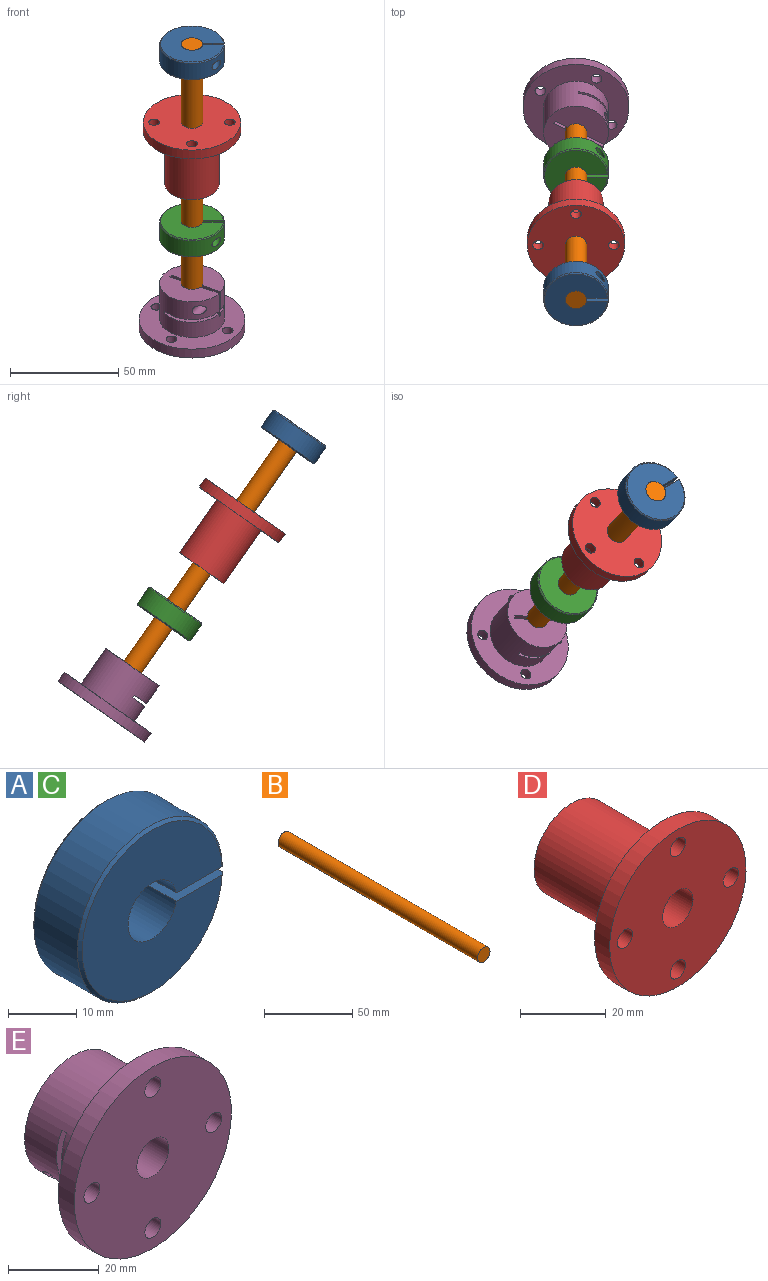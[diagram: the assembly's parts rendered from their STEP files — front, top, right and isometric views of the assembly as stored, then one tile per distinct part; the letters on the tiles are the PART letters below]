
ASSEMBLY  parts=5 mates=4
PART A: 10 faces, bbox 30x10x30 mm
  f0: cylinder r=5mm len=10mm, axis (0,-1,0), area 299.1mm2, adj f1,f3,f4,f5
  f1: plane 10.04x10mm, normal (0,0,1), area 87.6mm2, adj f0,f2,f4,f5,f7,f8,f9
  f2: cylinder r=15mm len=30mm, axis (0,-1,0), area 795.6mm2, adj f1,f3,f6,f7,f8,f9
  f3: plane 10.04x10mm, normal (0,0,-1), area 87.6mm2, adj f0,f2,f4,f5,f6,f8,f9
  f4: plane 29x28.98mm, normal (0,1,0), area 567.7mm2, adj f0,f1,f3,f9
  f5: plane 29x28.98mm, normal (0,-1,0), area 567.7mm2, adj f0,f1,f3,f8
  f6: cylinder r=2mm len=11.07mm, axis (0,0,1), area 112.5mm2, adj f2,f3
  f7: cylinder r=2mm len=11.07mm, axis (0,0,1), area 112.5mm2, adj f1,f2
  f8: cone r=15mm half-angle=45deg, axis (0,1,0), area 64.5mm2, adj f1,f2,f3,f5
  f9: cone r=14.5mm half-angle=45deg, axis (0,-1,0), area 64.5mm2, adj f1,f2,f3,f4
PART B: 3 faces, bbox 10x160x10 mm
  f0: cylinder r=5mm len=160mm, axis (0,-1,0), area 5026.5mm2, adj f1,f2
  f1: plane 10x10mm, normal (0,1,0), area 78.5mm2, adj f0
  f2: plane 10x10mm, normal (0,-1,0), area 78.5mm2, adj f0
PART C: same geometry as A
PART D: 10 faces, bbox 45x35x45 mm
  f0: cylinder r=22.5mm len=45mm, axis (0,-1,0), area 706.9mm2, adj f1,f2
  f1: plane 45x45mm, normal (0,1,0), area 1021mm2, adj f0,f4,f6,f7,f8,f9
  f2: plane 45x45mm, normal (0,-1,0), area 1433.4mm2, adj f0,f5,f6,f7,f8,f9
  f3: plane 25x25mm, normal (0,1,0), area 412.3mm2, adj f4,f5
  f4: cylinder r=12.5mm len=30mm, axis (0,-1,0), area 2356.2mm2, adj f1,f3
  f5: cylinder r=5mm len=35mm, axis (0,-1,0), area 1099.6mm2, adj f2,f3
  f6: cylinder r=2.5mm len=5mm, axis (0,1,0), area 78.5mm2, adj f1,f2
  f7: cylinder r=2.5mm len=5mm, axis (0,1,0), area 78.5mm2, adj f1,f2
  f8: cylinder r=2.5mm len=5mm, axis (0,1,0), area 78.5mm2, adj f1,f2
  f9: cylinder r=2.5mm len=5mm, axis (0,1,0), area 78.5mm2, adj f1,f2
PART E: 29 faces, bbox 49x25x49 mm
  f0: cylinder r=5mm len=10mm, axis (0,1,0), area 142mm2, adj f3,f14,f18,f23
  f1: plane 12.69x1.5mm, normal (0,0,-1), area 19mm2, adj f2,f3,f4,f23
  f2: plane 21.65x14.25mm, normal (0,1,0), area 225.3mm2, adj f1,f4,f5,f21,f23
  f3: plane 21.65x14.25mm, normal (0,-1,0), area 225.3mm2, adj f0,f1,f4,f18,f23
  f4: cylinder r=15mm len=30mm, axis (0,-1,0), area 1722mm2, adj f1,f2,f3,f7,f14,f15,f16,f17
  f5: cylinder r=5mm len=13.5mm, axis (0,1,0), area 418.8mm2, adj f2,f8,f16,f20,f21,f22,f23,f25
  f6: cylinder r=5mm len=10mm, axis (0,1,0), area 142mm2, adj f14,f17,f19,f25
  f7: plane 49x49mm, normal (0,1,0), area 1100.3mm2, adj f4,f9,f10,f11,f12,f13
  f8: plane 49x49mm, normal (0,-1,0), area 1728.7mm2, adj f5,f9,f10,f11,f12,f13
  f9: cylinder r=24.5mm len=49mm, axis (0,-1,0), area 769.7mm2, adj f7,f8
  f10: cylinder r=2.5mm len=5mm, axis (0,-1,0), area 78.5mm2, adj f7,f8
  f11: cylinder r=2.5mm len=5mm, axis (0,-1,0), area 78.5mm2, adj f7,f8
  f12: cylinder r=2.5mm len=5mm, axis (0,-1,0), area 78.5mm2, adj f7,f8
  f13: cylinder r=2.5mm len=5mm, axis (0,-1,0), area 78.5mm2, adj f7,f8
  f14: plane 30x29.98mm, normal (0,1,0), area 603.4mm2, adj f0,f4,f6,f18,f19,f23,f24,f25
  f15: plane 12.69x1.5mm, normal (0,0,-1), area 19mm2, adj f4,f16,f17,f25
  f16: plane 21.65x14.25mm, normal (0,1,0), area 225.3mm2, adj f4,f5,f15,f20,f25
  f17: plane 21.65x14.25mm, normal (0,-1,0), area 225.3mm2, adj f4,f6,f15,f19,f25
  f18: plane 10.04x10mm, normal (-1,0,0), area 80.7mm2, adj f0,f3,f4,f14,f28
  f19: plane 10.04x10mm, normal (1,0,0), area 80.7mm2, adj f4,f6,f14,f17,f27
  f20: plane 10.04x1.75mm, normal (1,0,0), area 17.6mm2, adj f4,f5,f16,f22
  f21: plane 10.04x1.75mm, normal (-1,0,0), area 17.6mm2, adj f2,f4,f5,f22
  f22: plane 10.06x1.5mm, normal (0,1,0), area 15mm2, adj f4,f5,f20,f21
  f23: plane 13.25x6.67mm, normal (-1,0,0), area 85.7mm2, adj f0,f1,f2,f3,f5,f14,f24,f26
  f24: plane 13.25x1.5mm, normal (0,0,-1), area 19.9mm2, adj f14,f23,f25,f26
  f25: plane 13.25x6.67mm, normal (1,0,0), area 85.7mm2, adj f5,f6,f14,f15,f16,f17,f24,f26
  f26: plane 6.67x1.5mm, normal (0,1,0), area 9.9mm2, adj f5,f23,f24,f25
  f27: cylinder r=2.5mm len=12.24mm, axis (1,0,0), area 159.7mm2, adj f4,f19
  f28: cylinder r=2.5mm len=12.24mm, axis (1,0,0), area 159.7mm2, adj f4,f18
PLACE A rot(axis=(-1,0,0),55deg) t=(56.97,-76.61,-6.34)mm
PLACE B rot(axis=(1,0,0),125deg) t=(56.97,15.17,-137.4)mm
PLACE C rot(axis=(1,0,0),125deg) t=(56.97,-13.51,-96.44)mm
PLACE D rot(axis=(-1,0,0),55deg) t=(56.97,-51.31,-42.45)mm
PLACE E rot(axis=(0.46,-0.41,-0.79),153.3deg) t=(56.97,15.17,-137.4)mm
MATE revolute B.f0 <-> E.f0  axis (0,0.57,-0.82) through (56.97,15.17,-137.4)mm
MATE revolute A.f0 <-> B.f0  axis (0,-0.57,0.82) through (56.97,-76.61,-6.34)mm
MATE cylindrical D.f0 <-> B.f0  axis (0,-0.57,0.82) through (56.97,-51.31,-42.45)mm
MATE revolute C.f0 <-> B.f0  axis (0,-0.57,0.82) through (56.97,-19.25,-88.25)mm
